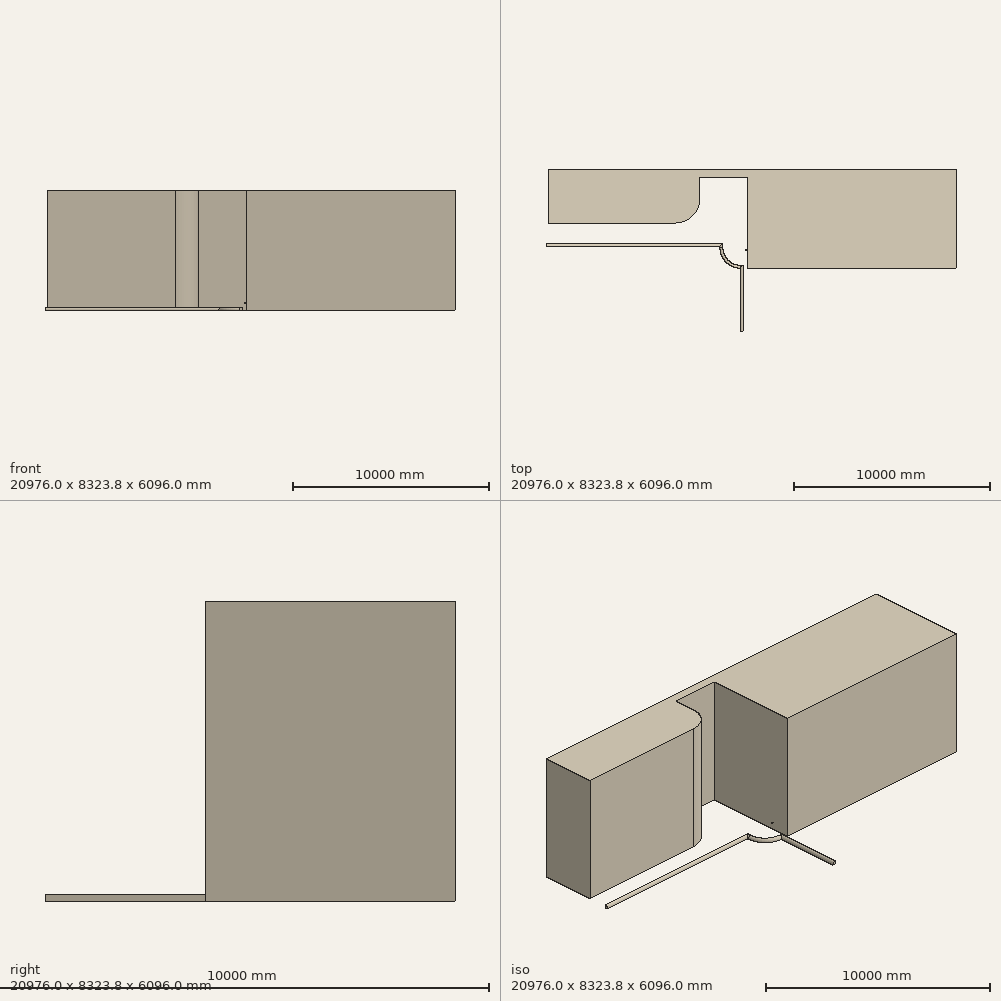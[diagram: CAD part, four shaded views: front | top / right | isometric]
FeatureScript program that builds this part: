
annotation { "Feature Type Name" : "Feature", "Feature Type Description" : "" }
export const myFeature = defineFeature(function(context is Context, id is Id, definition is map)
    precondition{}
    {
        {
            var Q0;
            Q0=qCreatedBy(makeId("Top.planeOp"),FACE);
            var sketch = newSketch(context, id + "F8", { "sketchPlane" : qUnion([Q0])});
            skLineSegment(sketch, "E0", {"start": v(-7759.81, 0) * mm, "end": v(0, 0) * mm});
            skLineSegment(sketch, "E1", {"start": v(0, 2308.06) * mm, "end": v(2438.4, 2308.06) * mm});
            skLineSegment(sketch, "E2", {"start": v(2438.4, 2308.06) * mm, "end": v(2438.4, -2310.78) * mm});
            skLineSegment(sketch, "E3", {"start": v(2438.4, -2310.78) * mm, "end": v(13126.7, -2310.78) * mm});
            skLineSegment(sketch, "E4", {"start": v(0, 2308.06) * mm, "end": v(0, 0) * mm});
            skLineSegment(sketch, "E5", {"start": v(-7849.32, -1044.65) * mm, "end": v(1180.88, -1044.65) * mm});
            skLineSegment(sketch, "E6", {"start": v(1180.88, -1044.65) * mm, "end": v(1180.88, -1244.17) * mm});
            skLineSegment(sketch, "E7", {"start": v(2095.28, -2158.57) * mm, "end": v(2221.43, -2158.57) * mm});
            skLineSegment(sketch, "E8", {"start": v(2221.43, -2158.57) * mm, "end": v(2221.43, -5567.8) * mm});
            skLineSegment(sketch, "E9", {"start": v(-7759.81, 0) * mm, "end": v(-7759.81, 2756) * mm});
            skLineSegment(sketch, "E10", {"start": v(-7759.81, 2756) * mm, "end": v(13126.7, 2756) * mm});
            skLineSegment(sketch, "E11", {"start": v(13126.7, 2756) * mm, "end": v(13126.7, -2310.78) * mm});
            skPoint(sketch, "E12.visualSharp", {"position": v(1180.88, -2158.57) * mm});
            skArc(sketch, "E12.filletArc", {"start": v(1180.88, -1244.17) * mm, "mid": v(1448.7, -1890.75) * mm, "end": v(2095.28, -2158.57) * mm});
            skLineSegment(sketch, "E13", {"start": v(-670.88, -108.53) * mm, "end": v(2350.44, -2114.17) * mm});
            skSolve(sketch);
        }
        {
            var Q0;
            Q0=makeQuery(id+"F8.imprint","IMPRINT",FACE,{"disambiguationData":[TD([[makeQuery(id+"F8.imprint","IMPRINT",EDGE,{"derivedFrom":sQuery(id+"F8.wireOp",EDGE,"E0")}),1.0]])]});
            extrude(context, id + "F0", {"entities" : qUnion([Q0]), "depth" : 6096 * mm});
        }
        {
            var Q0;
            Q0=sQuery(id+"F8.wireOp",VERTEX,"E5.start");
            var Q1;
            Q1=sQuery(id+"F8.wireOp",EDGE,"E5");
            cPlane(context, id + "F1", {"entities" : qUnion([Q0, Q1]), "cplaneType" : CPlaneType.LINE_POINT, "offset" : 25 * mm, "width" : 150 * mm, "height" : 150 * mm});
        }
        {
            var Q0;
            Q0=qCreatedBy(id+"F1.planeOp",FACE);
            var sketch = newSketch(context, id + "F2", { "sketchPlane" : qUnion([Q0])});
            skLineSegment(sketch, "E14", {"start": v(-1054.93, 0) * mm, "end": v(-1054.93, 149.56) * mm});
            skLineSegment(sketch, "E15", {"start": v(-1054.93, 0) * mm, "end": v(-1204.49, 0) * mm});
            skArc(sketch, "E16", {"start": v(-1054.93, 149.56) * mm, "mid": v(-1160.68, 105.76) * mm, "end": v(-1204.49, 0) * mm});
            skSolve(sketch);
        }
        {
            var Q0;
            Q0=qSketchRegion(id+"F2",true);
            var Q1;
            Q1=qConstructionFilter(qBodyType(qCreatedBy(id+"F2",EDGE),BodyType.WIRE),ConstructionObject.NO);
            var Q2;
            Q2=sQuery(id+"F8.wireOp",EDGE,"E5");
            var Q3;
            Q3=sQuery(id+"F8.wireOp",EDGE,"E6");
            var Q4;
            Q4=sQuery(id+"F8.wireOp",EDGE,"E12.filletArc");
            var Q5;
            Q5=sQuery(id+"F8.wireOp",EDGE,"E7");
            var Q6;
            Q6=sQuery(id+"F8.wireOp",EDGE,"E8");
            sweep(context, id + "F3", {"profiles" : qUnion([Q0]), "surfaceProfiles" : qUnion([Q1]), "path" : qUnion([Q2, Q3, Q4, Q5, Q6])});
        }
        {
            var Q0;
            Q0=makeQuery(id+"F0.opExtrude","SWEPT_FACE",FACE,{"disambiguationData":[OSD([sQuery(id+"F8.wireOp",EDGE,"E2")])]});
            var sketch = newSketch(context, id + "F4", { "sketchPlane" : qUnion([Q0])});
            skCircle(sketch, "E17", {"center": v(1402.42, 340.92) * mm, "radius": 25.4 * mm});
            skSolve(sketch);
        }
        {
            var Q0;
            Q0=qSketchRegion(id+"F4",true);
            extrude(context, id + "F5", {"entities" : qUnion([Q0]), "depth" : 101.6 * mm});
        }
        {
            var Q0;
            Q0=makeQuery(id+"F0.opExtrude","SWEPT_EDGE",EDGE,{"disambiguationData":[OSD([sQuery(id+"F8.wireOp",EDGE,"E0"),sQuery(id+"F8.wireOp",EDGE,"E4")])]});
            fillet(context, id + "F6", {"entities" : qUnion([Q0]), "radius" : 1219.2 * mm, "tangentPropagation" : true, "allowEdgeOverflow" : false});
        }
        {
            var Q0;
            Q0=sQuery(id+"F8.wireOp",EDGE,"E13");
            extrude(context, id + "F7", {"bodyType" : ToolBodyType.SURFACE, "surfaceEntities" : qUnion([Q0]), "depth" : 1828.8 * mm});
        }
    });
